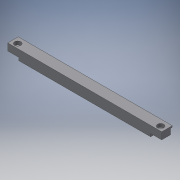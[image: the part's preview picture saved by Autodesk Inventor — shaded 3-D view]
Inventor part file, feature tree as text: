
AUTODESK INVENTOR PART (.ipt)
format: ipt  version: 2016 SP2 (Build 200236200, 236)  size: 141,312 bytes
history: native  units: mm
features: reference x8, extrude x4, sketch x4, mirror x1
ambient origin geometry x8: Origin, YZ Plane, XZ Plane, XY Plane, X Axis, Y Axis, Z Axis, Center Point
bodies: Volumenkörper1 (feature_tree)
feature tree (17):
  extrude  "Extrusion1"  Depth=10.0mm TaperAngle=0.0deg
  extrude  "Extrusion2"  Depth=5.0mm
  extrude  "Extrusion3"  Depth=3.1mm TaperAngle=0.0deg
  extrude  "Extrusion4"  Depth=3.4mm TaperAngle=0.0deg
  mirror  "Spiegeln1"
  sketch  "Skizze2"  dims[d0=69.4mm d1=0.0mm d2=10.0mm d3=0.0mm]
  reference  "Referenz1"
  reference  "Referenz2"
  reference  "Referenz3"
  reference  "Referenz4"
  reference  "Referenz5"
  reference  "Referenz6"
  reference  "Referenz7"
  sketch  "Skizze3"  dims[d4=5.7mm d5=5.0mm]
  reference  "Referenz8"
  sketch  "Skizze4"  dims[d6=4.0mm d7=3.1mm d8=0.0mm]
  sketch  "Skizze5"  dims[d9=3.0mm d10=3.4mm d11=0.0mm]
